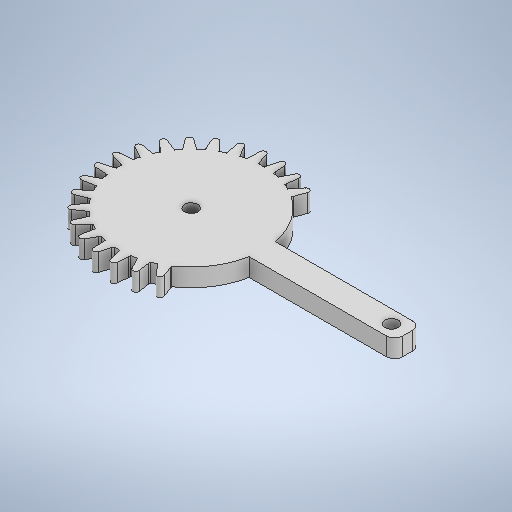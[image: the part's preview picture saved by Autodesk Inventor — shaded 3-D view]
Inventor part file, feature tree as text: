
AUTODESK INVENTOR PART (.ipt)
format: ipt  version: 2025.1 (Build 291241020, 241B)  size: 756,224 bytes
history: native  units: in
note: dims shown in document units (in); Inventor stores cm internally (conversion verified against a paired STEP export)
features: sketch x15, extrude x14, other x3, fillet x2, pattern_circular x1
ambient origin geometry x8: Origin, YZ Plane, XZ Plane, XY Plane, X Axis, Y Axis, Z Axis, Center Point
bodies: Solid1 (feature_tree)
feature tree (35):
  other  "servoMoldAssembly.iam"
  other  "block.ipt:1"
  other  "sg90horn.ipt:1"
  extrude  "Extrusion1"  Depth=0.3937in TaperAngle=0.0deg
  extrude  "Extrusion2"  Depth=0.3937in TaperAngle=0.0deg
  extrude  "Extrusion3"  Depth=0.0591in TaperAngle=0.0deg
  extrude  "Extrusion4"  Depth=0.0591in TaperAngle=0.0deg
  extrude  "Extrusion5"  Depth=1.9685in
  extrude  "Extrusion6"  Depth=0.3937in TaperAngle=0.0deg
  extrude  "Extrusion7"  Depth=0.3937in TaperAngle=0.0deg
  extrude  "Extrusion8"  Depth=0.1299in
  extrude  "Extrusion10"  Depth=0.0787in TaperAngle=0.0deg
  extrude  "Extrusion11"  Depth=0.0787in TaperAngle=0.0deg
  fillet  "Fillet1"  Radius=0.0787in
  extrude  "Extrusion12"  Depth=0.8268in
  fillet  "Fillet2"  Radius=1.1934in
  extrude  "Extrusion13"  TaperAngle=90.0deg  [1 undecoded]
  pattern_circular  "Circular Pattern2"  Count=20 Angle=240.0deg
  extrude  "Extrusion14"  Depth=0.3937in
  extrude  "Extrusion15"  [1 undecoded]
  sketch  "Sketch18"  dims[d53=0.3937in d54=0.0in]
  sketch  "Sketch3"  dims[d0=0.3937in d1=0.3937in d2=0.0in]
  sketch  "Sketch4"  dims[d3=0.2795in d4=0.3937in d5=0.0in]
  sketch  "Sketch5"  dims[d6=0.0591in d7=0.0in d8=0.0591in d9=0.0in]
  sketch  "Sketch6"  dims[d10=0.0591in d11=0.0in d12=0.0591in d13=0.0in]
  sketch  "Sketch7"  dims[d14=1.4173in d15=1.9685in]
  sketch  "Sketch8"  dims[d16=0.0in d17=0.3937in d18=0.0in]
  sketch  "Sketch9"  dims[d19=0.3937in d20=0.0in d29=0.2362in d30=0.0in]
  sketch  "Sketch10"  dims[d31=0.2362in d32=0.1299in]
  sketch  "Sketch12"  dims[d33=0.0787in d34=0.2362in d35=0.0in]
  sketch  "Sketch13"  dims[d36=0.0787in d37=0.2362in d38=0.0in d39=0.0787in]
  sketch  "Sketch14"  dims[d40=0.0984in d41=0.8268in d42=1.1934in]
  sketch  "Sketch15"  dims[d43=0.0591in d44=90.0deg]
  sketch  "Sketch16"  dims[d45=0.3937in d46=0.0in d47=7.874in d48=240.0deg]
  sketch  "Sketch17"  dims[d50=0.3937in d51=0.0in d52=0.1299in]
note: 2 required parameter values undecoded (feature->parameter linkage not recoverable at this tier; creation-order binding heuristic only, values carry confidence <= 0.55)
